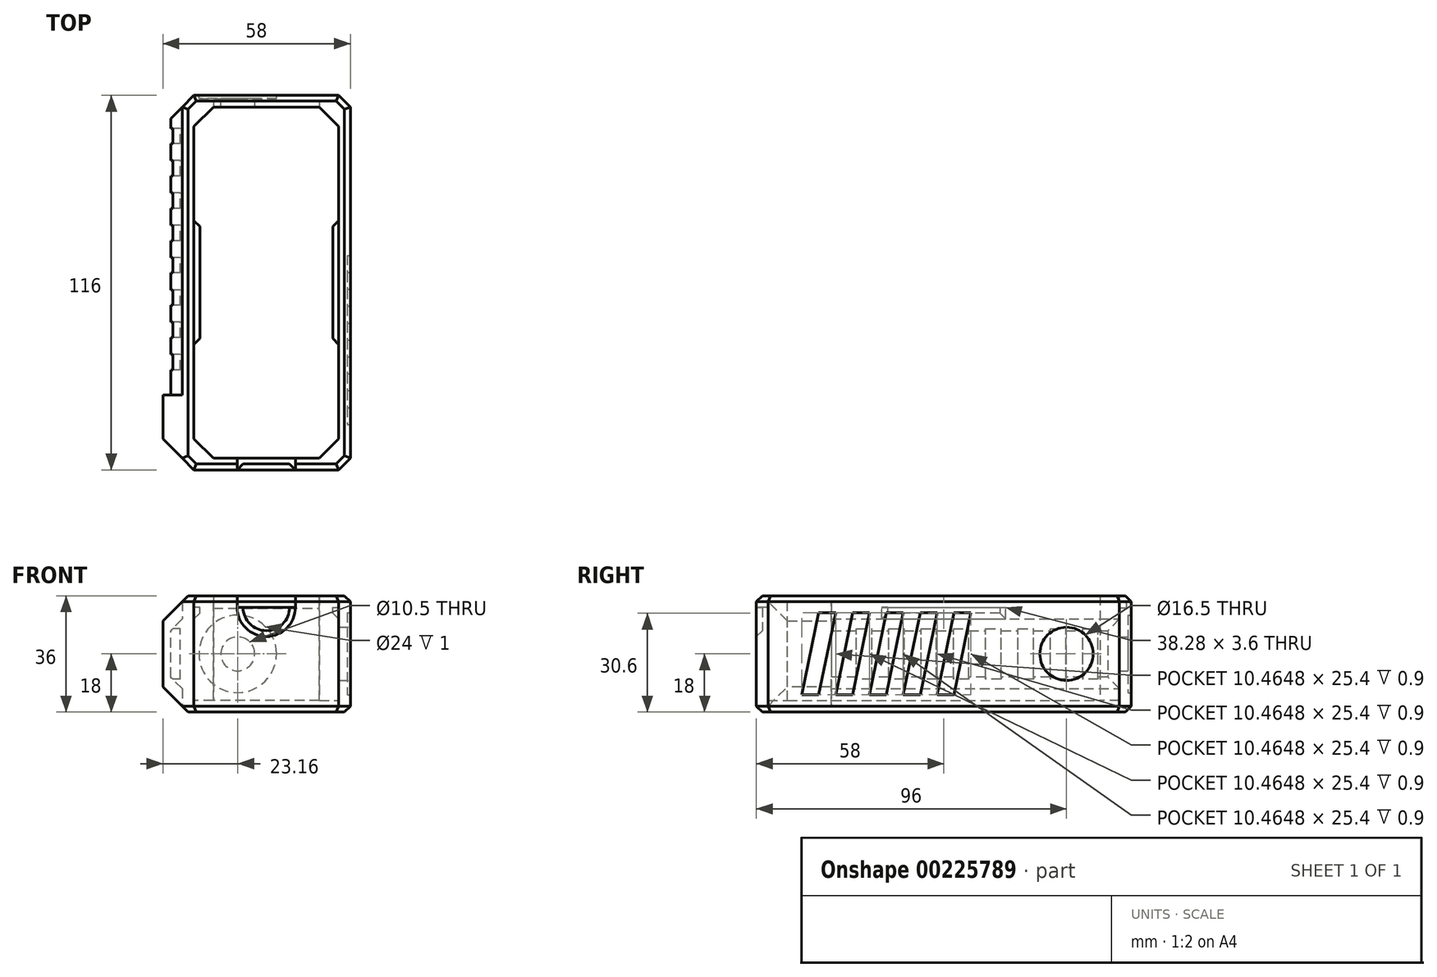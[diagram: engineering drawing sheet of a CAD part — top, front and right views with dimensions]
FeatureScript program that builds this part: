
annotation { "Feature Type Name" : "Feature", "Feature Type Description" : "" }
export const myFeature = defineFeature(function(context is Context, id is Id, definition is map)
    precondition{}
    {
        {
            assignVariable(context, id + "F0", {"name" : "O", "anyValue" : 3.6});
        }
        {
            assignVariable(context, id + "F1", {"name" : "H", "anyValue" : 36});
        }
        {
            var Q0;
            Q0=qCreatedBy(makeId("Top.planeOp"),FACE);
            var sketch = newSketch(context, id + "F2", { "sketchPlane" : qUnion([Q0])});
            skLineSegment(sketch, "E0.bottom", {"start": v(26, -58) * mm, "end": v(-26, -58) * mm});
            skLineSegment(sketch, "E0.top", {"start": v(26, 58) * mm, "end": v(-26, 58) * mm});
            skLineSegment(sketch, "E0.left", {"start": v(26, -58) * mm, "end": v(26, 58) * mm});
            skLineSegment(sketch, "E0.right", {"start": v(-26, -58) * mm, "end": v(-26, 58) * mm});
            skPoint(sketch, "E0.middle", {"position": v(0, 0) * mm});
            skLineSegment(sketch, "E1.0", {"start": v(22.4, 54.4) * mm, "end": v(-22.4, 54.4) * mm});
            skLineSegment(sketch, "E1.1", {"start": v(22.4, -54.4) * mm, "end": v(22.4, 54.4) * mm});
            skLineSegment(sketch, "E1.2", {"start": v(22.4, -54.4) * mm, "end": v(-22.4, -54.4) * mm});
            skLineSegment(sketch, "E1.3", {"start": v(-22.4, -54.4) * mm, "end": v(-22.4, 54.4) * mm});
            skSolve(sketch);
        }
        {
            var Q0;
            Q0=makeQuery(id+"F2.imprint","IMPRINT",FACE,{"disambiguationData":[TD([[makeQuery(id+"F2.imprint","IMPRINT",EDGE,{"derivedFrom":sQuery(id+"F2.wireOp",EDGE,"E0.bottom")}),-1.0]])]});
            extrude(context, id + "F3", {"entities" : qUnion([Q0]), "depth" : (getVariable(context, 'H')) * mm});
        }
        {
            var Q0;
            Q0=makeQuery(id+"F2.imprint","IMPRINT",FACE,{"disambiguationData":[TD([[makeQuery(id+"F2.imprint","IMPRINT",EDGE,{"derivedFrom":sQuery(id+"F2.wireOp",EDGE,"E1.0")}),1.0]])]});
            extrude(context, id + "F4", {"entities" : qUnion([Q0]), "operationType" : NewBodyOperationType.ADD, "depth" : (getVariable(context, 'O')) * mm});
        }
        {
            var Q0;
            Q0=makeQuery(id+"F3.opExtrude","SWEPT_FACE",FACE,{"disambiguationData":[OSD([sQuery(id+"F2.wireOp",EDGE,"E0.left")])]});
            var sketch = newSketch(context, id + "F5", { "sketchPlane" : qUnion([Q0])});
            skCircle(sketch, "E2", {"center": v(38, 18) * mm, "radius": 8.25 * mm});
            skSolve(sketch);
        }
        {
            var Q0;
            Q0=makeQuery(id+"F3.opExtrude","SWEPT_FACE",FACE,{"disambiguationData":[OSD([sQuery(id+"F2.wireOp",EDGE,"E0.top")])]});
            var sketch = newSketch(context, id + "F6", { "sketchPlane" : qUnion([Q0])});
            skCircle(sketch, "E3", {"center": v(8.84, 18) * mm, "radius": 5.25 * mm});
            skCircle(sketch, "E4", {"center": v(8.84, 18) * mm, "radius": 12 * mm});
            skSolve(sketch);
        }
        {
            var Q0;
            Q0=makeQuery(id+"F3.opExtrude","SWEPT_EDGE",EDGE,{"disambiguationData":[OSD([sQuery(id+"F2.wireOp",EDGE,"E0.bottom"),sQuery(id+"F2.wireOp",EDGE,"E0.right")])]});
            var Q1;
            Q1=makeQuery(id+"F3.opExtrude","SWEPT_EDGE",EDGE,{"disambiguationData":[OSD([sQuery(id+"F2.wireOp",EDGE,"E0.bottom"),sQuery(id+"F2.wireOp",EDGE,"E0.left")])]});
            var Q2;
            Q2=makeQuery(id+"F3.opExtrude","SWEPT_EDGE",EDGE,{"disambiguationData":[OSD([sQuery(id+"F2.wireOp",EDGE,"E0.top"),sQuery(id+"F2.wireOp",EDGE,"E0.left")])]});
            var Q3;
            Q3=makeQuery(id+"F3.opExtrude","SWEPT_EDGE",EDGE,{"disambiguationData":[OSD([sQuery(id+"F2.wireOp",EDGE,"E0.top"),sQuery(id+"F2.wireOp",EDGE,"E0.right")])]});
            chamfer(context, id + "F7", {"entities" : qUnion([Q0, Q1, Q2, Q3]), "width" : (getVariable(context, 'O')) * mm, "tangentPropagation" : true});
        }
        {
            var Q0;
            Q0=makeQuery(id+"F3.opExtrude","SWEPT_EDGE",EDGE,{"disambiguationData":[OSD([sQuery(id+"F2.wireOp",EDGE,"E1.0"),sQuery(id+"F2.wireOp",EDGE,"E1.3")])]});
            var Q1;
            Q1=makeQuery(id+"F3.opExtrude","SWEPT_EDGE",EDGE,{"disambiguationData":[OSD([sQuery(id+"F2.wireOp",EDGE,"E1.0"),sQuery(id+"F2.wireOp",EDGE,"E1.1")])]});
            var Q2;
            Q2=makeQuery(id+"F3.opExtrude","SWEPT_EDGE",EDGE,{"disambiguationData":[OSD([sQuery(id+"F2.wireOp",EDGE,"E1.2"),sQuery(id+"F2.wireOp",EDGE,"E1.3")])]});
            var Q3;
            Q3=makeQuery(id+"F3.opExtrude","SWEPT_EDGE",EDGE,{"disambiguationData":[OSD([sQuery(id+"F2.wireOp",EDGE,"E1.1"),sQuery(id+"F2.wireOp",EDGE,"E1.2")])]});
            chamfer(context, id + "F8", {"entities" : qUnion([Q0, Q1, Q2, Q3]), "width" : (getVariable(context, 'O') * 1.67) * mm, "tangentPropagation" : true});
        }
        {
            var Q0;
            Q0=makeQuery(id+"F6.imprint","IMPRINT",FACE,{"disambiguationData":[TD([[makeQuery(id+"F6.imprint","IMPRINT",EDGE,{"derivedFrom":sQuery(id+"F6.wireOp",EDGE,"E3")}),1.0]])]});
            extrude(context, id + "F9", {"entities" : qUnion([Q0]), "operationType" : NewBodyOperationType.REMOVE, "oppositeDirection" : true, "depth" : (getVariable(context, 'O')) * mm});
        }
        {
            var Q0;
            Q0=makeQuery(id+"F5.imprint","IMPRINT",FACE,{"disambiguationData":[TD([[makeQuery(id+"F5.imprint","IMPRINT",EDGE,{"derivedFrom":sQuery(id+"F5.wireOp",EDGE,"E2")}),1.0]])]});
            extrude(context, id + "F10", {"entities" : qUnion([Q0]), "operationType" : NewBodyOperationType.REMOVE, "oppositeDirection" : true, "depth" : (getVariable(context, 'O')) * mm});
        }
        {
            var Q0;
            Q0=makeQuery(id+"F3.opExtrude","SWEPT_FACE",FACE,{"disambiguationData":[OSD([sQuery(id+"F2.wireOp",EDGE,"E0.bottom")])]});
            var sketch = newSketch(context, id + "F11", { "sketchPlane" : qUnion([Q0])});
            skLineSegment(sketch, "E5.bottom", {"start": v(9, 32.4) * mm, "end": v(-9, 32.4) * mm});
            skLineSegment(sketch, "E5.top", {"start": v(9, 36) * mm, "end": v(-9, 36) * mm});
            skLineSegment(sketch, "E5.left", {"start": v(9, 32.4) * mm, "end": v(9, 36) * mm});
            skLineSegment(sketch, "E5.right", {"start": v(-9, 32.4) * mm, "end": v(-9, 36) * mm});
            skPoint(sketch, "E5.middle", {"position": v(0, 34.2) * mm});
            skPoint(sketch, "E5.middle.positionSnap0", {"position": v(0, 0) * mm});
            skPoint(sketch, "E5.centerSnap0", {"position": v(0, 0) * mm});
            skArc(sketch, "E6", {"start": v(-9, 32.4) * mm, "mid": v(0, 23.4) * mm, "end": v(9, 32.4) * mm});
            skSolve(sketch);
        }
        {
            var Q0;
            Q0=makeQuery(id+"F11.imprint","IMPRINT",FACE,{"disambiguationData":[TD([[makeQuery(id+"F11.imprint","IMPRINT",EDGE,{"derivedFrom":sQuery(id+"F11.wireOp",EDGE,"E5.bottom")}),-1.0]])]});
            extrude(context, id + "F12", {"entities" : qUnion([Q0]), "operationType" : NewBodyOperationType.REMOVE, "oppositeDirection" : true, "depth" : (getVariable(context, 'O')) * mm});
        }
        {
            var Q0;
            Q0=makeQuery(id+"F3.opExtrude","SWEPT_FACE",FACE,{"disambiguationData":[OSD([sQuery(id+"F2.wireOp",EDGE,"E1.0")])]});
            var sketch = newSketch(context, id + "F13", { "sketchPlane" : qUnion([Q0])});
            skLineSegment(sketch, "E7.bottom", {"start": v(-16.4, 34.2) * mm, "end": v(16.4, 34.2) * mm});
            skLineSegment(sketch, "E7.top", {"start": v(-16.4, 32.2) * mm, "end": v(16.4, 32.2) * mm});
            skLineSegment(sketch, "E7.left", {"start": v(-16.4, 34.2) * mm, "end": v(-16.4, 32.2) * mm});
            skLineSegment(sketch, "E7.right", {"start": v(16.4, 34.2) * mm, "end": v(16.4, 32.2) * mm});
            skSolve(sketch);
        }
        {
            var Q0;
            Q0=makeQuery(id+"F13.imprint","IMPRINT",FACE,{"disambiguationData":[TD([[makeQuery(id+"F13.imprint","IMPRINT",EDGE,{"derivedFrom":sQuery(id+"F13.wireOp",EDGE,"E7.bottom")}),-1.0]])]});
            extrude(context, id + "F14", {"entities" : qUnion([Q0]), "operationType" : NewBodyOperationType.REMOVE, "oppositeDirection" : true, "depth" : 2.1 * mm});
        }
        {
            var Q0;
            Q0=makeQuery(id+"F6.imprint","IMPRINT",FACE,{"disambiguationData":[TD([[makeQuery(id+"F6.imprint","IMPRINT",EDGE,{"derivedFrom":sQuery(id+"F6.wireOp",EDGE,"E3")}),-1.0]])]});
            extrude(context, id + "F15", {"entities" : qUnion([Q0]), "operationType" : NewBodyOperationType.REMOVE, "oppositeDirection" : true, "depth" : 1 * mm});
        }
        {
            var Q0;
            Q0=makeQuery(id+"F14.boolean.opBoolean","COPY",EDGE,{"derivedFrom":makeQuery(id+"F14.opExtrude","CAP_EDGE",EDGE,{"disambiguationData":[OSD([sQuery(id+"F13.wireOp",EDGE,"E7.bottom")])],"isStart":false})});
            fillet(context, id + "F16", {"entities" : qUnion([Q0]), "radius" : 0.5 * mm, "tangentPropagation" : true, "allowEdgeOverflow" : false});
        }
        {
            var Q0;
            Q0=makeQuery(id+"F3.opExtrude","SWEPT_FACE",FACE,{"disambiguationData":[OSD([sQuery(id+"F2.wireOp",EDGE,"E1.1")])]});
            var sketch = newSketch(context, id + "F17", { "sketchPlane" : qUnion([Q0])});
            skLineSegment(sketch, "E8.bottom", {"start": v(19.14, 28.8) * mm, "end": v(-19.14, 28.8) * mm});
            skLineSegment(sketch, "E8.top", {"start": v(19.14, 32.4) * mm, "end": v(-19.14, 32.4) * mm});
            skLineSegment(sketch, "E8.left", {"start": v(19.14, 28.8) * mm, "end": v(19.14, 32.4) * mm});
            skLineSegment(sketch, "E8.right", {"start": v(-19.14, 28.8) * mm, "end": v(-19.14, 32.4) * mm});
            skPoint(sketch, "E8.middle", {"position": v(0, 30.6) * mm});
            skSolve(sketch);
        }
        {
            var Q0;
            Q0=makeQuery(id+"F3.opExtrude","SWEPT_FACE",FACE,{"disambiguationData":[OSD([sQuery(id+"F2.wireOp",EDGE,"E1.3")])]});
            var sketch = newSketch(context, id + "F18", { "sketchPlane" : qUnion([Q0])});
            skLineSegment(sketch, "E9.bottom", {"start": v(19.14, 28.8) * mm, "end": v(-19.14, 28.8) * mm});
            skLineSegment(sketch, "E9.top", {"start": v(19.14, 32.4) * mm, "end": v(-19.14, 32.4) * mm});
            skLineSegment(sketch, "E9.left", {"start": v(19.14, 28.8) * mm, "end": v(19.14, 32.4) * mm});
            skLineSegment(sketch, "E9.right", {"start": v(-19.14, 28.8) * mm, "end": v(-19.14, 32.4) * mm});
            skPoint(sketch, "E9.middle", {"position": v(0, 30.6) * mm});
            skSolve(sketch);
        }
        {
            var Q0;
            Q0=makeQuery(id+"F17.imprint","IMPRINT",FACE,{"disambiguationData":[TD([[makeQuery(id+"F17.imprint","IMPRINT",EDGE,{"derivedFrom":sQuery(id+"F17.wireOp",EDGE,"E8.bottom")}),-1.0]])]});
            extrude(context, id + "F19", {"entities" : qUnion([Q0]), "operationType" : NewBodyOperationType.ADD, "depth" : (getVariable(context, 'O') * .5) * mm});
        }
        {
            var Q0;
            Q0=makeQuery(id+"F18.imprint","IMPRINT",FACE,{"disambiguationData":[TD([[makeQuery(id+"F18.imprint","IMPRINT",EDGE,{"derivedFrom":sQuery(id+"F18.wireOp",EDGE,"E9.bottom")}),-1.0]])]});
            extrude(context, id + "F20", {"entities" : qUnion([Q0]), "operationType" : NewBodyOperationType.ADD, "depth" : (getVariable(context, 'O') * .5) * mm});
        }
        {
            var Q0;
            Q0=makeQuery(id+"F20.opExtrude","CAP_EDGE",EDGE,{"disambiguationData":[OSD([sQuery(id+"F18.wireOp",EDGE,"E9.right")])],"isStart":false});
            var Q1;
            Q1=makeQuery(id+"F20.opExtrude","CAP_EDGE",EDGE,{"disambiguationData":[OSD([sQuery(id+"F18.wireOp",EDGE,"E9.bottom")])],"isStart":false});
            var Q2;
            Q2=makeQuery(id+"F20.opExtrude","CAP_EDGE",EDGE,{"disambiguationData":[OSD([sQuery(id+"F18.wireOp",EDGE,"E9.left")])],"isStart":false});
            var Q3;
            Q3=makeQuery(id+"FUkj4zLFzn2cjNl_1.opExtrude","CAP_EDGE",EDGE,{"disambiguationData":[OSD([sQuery(id+"FduqIQM7QhTX7Re_1.wireOp",EDGE,"Uwhg5jXr-3Yt5-poT9-xr3U-90L54EeIlBer.right")])],"isStart":false});
            var Q4;
            Q4=makeQuery(id+"FUkj4zLFzn2cjNl_1.opExtrude","CAP_EDGE",EDGE,{"disambiguationData":[OSD([sQuery(id+"FduqIQM7QhTX7Re_1.wireOp",EDGE,"Uwhg5jXr-3Yt5-poT9-xr3U-90L54EeIlBer.left")])],"isStart":false});
            var Q5;
            Q5=makeQuery(id+"FUkj4zLFzn2cjNl_1.opExtrude","CAP_EDGE",EDGE,{"disambiguationData":[OSD([sQuery(id+"FduqIQM7QhTX7Re_1.wireOp",EDGE,"Uwhg5jXr-3Yt5-poT9-xr3U-90L54EeIlBer.bottom")])],"isStart":false});
            var Q6;
            Q6=makeQuery(id+"F19.opExtrude","CAP_EDGE",EDGE,{"disambiguationData":[OSD([sQuery(id+"F17.wireOp",EDGE,"E8.right")])],"isStart":false});
            var Q7;
            Q7=makeQuery(id+"F19.opExtrude","CAP_EDGE",EDGE,{"disambiguationData":[OSD([sQuery(id+"F17.wireOp",EDGE,"E8.bottom")])],"isStart":false});
            var Q8;
            Q8=makeQuery(id+"F19.opExtrude","CAP_EDGE",EDGE,{"disambiguationData":[OSD([sQuery(id+"F17.wireOp",EDGE,"E8.left")])],"isStart":false});
            chamfer(context, id + "F21", {"entities" : qUnion([Q0, Q1, Q2, Q3, Q4, Q5, Q6, Q7, Q8]), "width" : (getVariable(context, 'O') * 0.5) * mm, "tangentPropagation" : true});
        }
        {
            var Q0;
            Q0=makeQuery(id+"F3.opExtrude","SWEPT_FACE",FACE,{"disambiguationData":[OSD([sQuery(id+"F2.wireOp",EDGE,"E1.2")])]});
            var sketch = newSketch(context, id + "F22", { "sketchPlane" : qUnion([Q0])});
            skSolve(sketch);
        }
        {
            var Q0;
            Q0=makeQuery(id+"F11.imprint","IMPRINT",FACE,{"disambiguationData":[TD([[makeQuery(id+"F11.imprint","IMPRINT",EDGE,{"derivedFrom":sQuery(id+"F11.wireOp",EDGE,"E5.bottom")}),1.0]])]});
            extrude(context, id + "F23", {"entities" : qUnion([Q0]), "operationType" : NewBodyOperationType.REMOVE, "oppositeDirection" : true, "depth" : (getVariable(context, 'O') / 2) * mm});
        }
        {
            var Q0;
            Q0=makeQuery(id+"F23.boolean.opBoolean","COPY",EDGE,{"derivedFrom":makeQuery(id+"F23.opExtrude","CAP_EDGE",EDGE,{"disambiguationData":[OSD([sQuery(id+"F11.wireOp",EDGE,"E6")])],"isStart":false})});
            chamfer(context, id + "F24", {"entities" : qUnion([Q0]), "width" : 1.8 * mm, "tangentPropagation" : true});
        }
        {
            var Q0;
            {var subQ0=sQuery(id+"F2.wireOp",EDGE,"E0.bottom");Q0=makeQuery(id+"F12.boolean.opBoolean","SPLIT",EDGE,{"disambiguationData":[TD([makeQuery(id+"F12.opExtrude","SWEPT_FACE",FACE,{"disambiguationData":[OSD([sQuery(id+"F11.wireOp",EDGE,"E5.right")])]})])],"derivedFrom":makeQuery(id+"F3.opExtrude","CAP_EDGE",EDGE,{"disambiguationData":[OSD([subQ0])],"isStart":false})});}
            var Q1;
            {var subQ0=sQuery(id+"F2.wireOp",EDGE,"E0.right");var subQ1=sQuery(id+"F2.wireOp",EDGE,"E0.bottom");Q1=makeQuery(id+"F7.opChamfer","BLEND_EDGE",EDGE,{"blendedFrom":[makeQuery(id+"F3.opExtrude","SWEPT_EDGE",EDGE,{"disambiguationData":[OSD([subQ1,subQ0])]}),makeQuery(id+"F3.opExtrude","CAP_FACE",FACE,{"disambiguationData":[OSD([subQ1,sQuery(id+"F2.wireOp",EDGE,"E0.top"),sQuery(id+"F2.wireOp",EDGE,"E0.left"),subQ0,sQuery(id+"F2.wireOp",EDGE,"E1.0"),sQuery(id+"F2.wireOp",EDGE,"E1.1"),sQuery(id+"F2.wireOp",EDGE,"E1.2"),sQuery(id+"F2.wireOp",EDGE,"E1.3")])],"isStart":false})],"blendedInto":[makeQuery(id+"F3.opExtrude","CAP_FACE",FACE,{"disambiguationData":[OSD([subQ1,sQuery(id+"F2.wireOp",EDGE,"E0.top"),sQuery(id+"F2.wireOp",EDGE,"E0.left"),subQ0,sQuery(id+"F2.wireOp",EDGE,"E1.0"),sQuery(id+"F2.wireOp",EDGE,"E1.1"),sQuery(id+"F2.wireOp",EDGE,"E1.2"),sQuery(id+"F2.wireOp",EDGE,"E1.3")])],"isStart":false})]});}
            var Q2;
            Q2=makeQuery(id+"F3.opExtrude","CAP_EDGE",EDGE,{"disambiguationData":[OSD([sQuery(id+"F2.wireOp",EDGE,"E0.right")])],"isStart":false});
            var Q3;
            {var subQ0=sQuery(id+"F2.wireOp",EDGE,"E0.right");var subQ1=sQuery(id+"F2.wireOp",EDGE,"E0.top");Q3=makeQuery(id+"F7.opChamfer","BLEND_EDGE",EDGE,{"blendedFrom":[makeQuery(id+"F3.opExtrude","SWEPT_EDGE",EDGE,{"disambiguationData":[OSD([subQ1,subQ0])]}),makeQuery(id+"F3.opExtrude","CAP_FACE",FACE,{"disambiguationData":[OSD([sQuery(id+"F2.wireOp",EDGE,"E0.bottom"),subQ1,sQuery(id+"F2.wireOp",EDGE,"E0.left"),subQ0,sQuery(id+"F2.wireOp",EDGE,"E1.0"),sQuery(id+"F2.wireOp",EDGE,"E1.1"),sQuery(id+"F2.wireOp",EDGE,"E1.2"),sQuery(id+"F2.wireOp",EDGE,"E1.3")])],"isStart":false})],"blendedInto":[makeQuery(id+"F3.opExtrude","CAP_FACE",FACE,{"disambiguationData":[OSD([sQuery(id+"F2.wireOp",EDGE,"E0.bottom"),subQ1,sQuery(id+"F2.wireOp",EDGE,"E0.left"),subQ0,sQuery(id+"F2.wireOp",EDGE,"E1.0"),sQuery(id+"F2.wireOp",EDGE,"E1.1"),sQuery(id+"F2.wireOp",EDGE,"E1.2"),sQuery(id+"F2.wireOp",EDGE,"E1.3")])],"isStart":false})]});}
            var Q4;
            Q4=makeQuery(id+"F3.opExtrude","CAP_EDGE",EDGE,{"disambiguationData":[OSD([sQuery(id+"F2.wireOp",EDGE,"E0.top")])],"isStart":false});
            var Q5;
            {var subQ0=sQuery(id+"F2.wireOp",EDGE,"E0.left");var subQ1=sQuery(id+"F2.wireOp",EDGE,"E0.top");Q5=makeQuery(id+"F7.opChamfer","BLEND_EDGE",EDGE,{"blendedFrom":[makeQuery(id+"F3.opExtrude","SWEPT_EDGE",EDGE,{"disambiguationData":[OSD([subQ1,subQ0])]}),makeQuery(id+"F3.opExtrude","CAP_FACE",FACE,{"disambiguationData":[OSD([sQuery(id+"F2.wireOp",EDGE,"E0.bottom"),subQ1,subQ0,sQuery(id+"F2.wireOp",EDGE,"E0.right"),sQuery(id+"F2.wireOp",EDGE,"E1.0"),sQuery(id+"F2.wireOp",EDGE,"E1.1"),sQuery(id+"F2.wireOp",EDGE,"E1.2"),sQuery(id+"F2.wireOp",EDGE,"E1.3")])],"isStart":false})],"blendedInto":[makeQuery(id+"F3.opExtrude","CAP_FACE",FACE,{"disambiguationData":[OSD([sQuery(id+"F2.wireOp",EDGE,"E0.bottom"),subQ1,subQ0,sQuery(id+"F2.wireOp",EDGE,"E0.right"),sQuery(id+"F2.wireOp",EDGE,"E1.0"),sQuery(id+"F2.wireOp",EDGE,"E1.1"),sQuery(id+"F2.wireOp",EDGE,"E1.2"),sQuery(id+"F2.wireOp",EDGE,"E1.3")])],"isStart":false})]});}
            var Q6;
            Q6=makeQuery(id+"F3.opExtrude","CAP_EDGE",EDGE,{"disambiguationData":[OSD([sQuery(id+"F2.wireOp",EDGE,"E0.left")])],"isStart":false});
            var Q7;
            {var subQ0=sQuery(id+"F2.wireOp",EDGE,"E0.left");var subQ1=sQuery(id+"F2.wireOp",EDGE,"E0.bottom");Q7=makeQuery(id+"F7.opChamfer","BLEND_EDGE",EDGE,{"blendedFrom":[makeQuery(id+"F3.opExtrude","SWEPT_EDGE",EDGE,{"disambiguationData":[OSD([subQ1,subQ0])]}),makeQuery(id+"F3.opExtrude","CAP_FACE",FACE,{"disambiguationData":[OSD([subQ1,sQuery(id+"F2.wireOp",EDGE,"E0.top"),subQ0,sQuery(id+"F2.wireOp",EDGE,"E0.right"),sQuery(id+"F2.wireOp",EDGE,"E1.0"),sQuery(id+"F2.wireOp",EDGE,"E1.1"),sQuery(id+"F2.wireOp",EDGE,"E1.2"),sQuery(id+"F2.wireOp",EDGE,"E1.3")])],"isStart":false})],"blendedInto":[makeQuery(id+"F3.opExtrude","CAP_FACE",FACE,{"disambiguationData":[OSD([subQ1,sQuery(id+"F2.wireOp",EDGE,"E0.top"),subQ0,sQuery(id+"F2.wireOp",EDGE,"E0.right"),sQuery(id+"F2.wireOp",EDGE,"E1.0"),sQuery(id+"F2.wireOp",EDGE,"E1.1"),sQuery(id+"F2.wireOp",EDGE,"E1.2"),sQuery(id+"F2.wireOp",EDGE,"E1.3")])],"isStart":false})]});}
            var Q8;
            {var subQ0=sQuery(id+"F2.wireOp",EDGE,"E0.bottom");Q8=makeQuery(id+"F12.boolean.opBoolean","SPLIT",EDGE,{"disambiguationData":[TD([makeQuery(id+"F12.opExtrude","SWEPT_FACE",FACE,{"disambiguationData":[OSD([sQuery(id+"F11.wireOp",EDGE,"E5.left")])]})])],"derivedFrom":makeQuery(id+"F3.opExtrude","CAP_EDGE",EDGE,{"disambiguationData":[OSD([subQ0])],"isStart":false})});}
            var Q9;
            {var subQ0=sQuery(id+"F2.wireOp",EDGE,"E1.3");var subQ1=sQuery(id+"F2.wireOp",EDGE,"E1.2");var subQ2=sQuery(id+"F2.wireOp",EDGE,"E1.1");var subQ3=sQuery(id+"F2.wireOp",EDGE,"E1.0");Q9=makeQuery(id+"F4.boolean.opBoolean","MERGE",FACE,{"derivedFrom":[makeQuery(id+"F3.opExtrude","CAP_FACE",FACE,{"disambiguationData":[OSD([sQuery(id+"F2.wireOp",EDGE,"E0.bottom"),sQuery(id+"F2.wireOp",EDGE,"E0.top"),sQuery(id+"F2.wireOp",EDGE,"E0.left"),sQuery(id+"F2.wireOp",EDGE,"E0.right"),subQ3,subQ2,subQ1,subQ0])],"isStart":true}),makeQuery(id+"F4.opExtrude","CAP_FACE",FACE,{"disambiguationData":[OSD([subQ3,subQ2,subQ1,subQ0])],"isStart":true})]});}
            chamfer(context, id + "F25", {"entities" : qUnion([Q0, Q1, Q2, Q3, Q4, Q5, Q6, Q7, Q8, Q9]), "width" : (getVariable(context, 'O') / 2) * mm, "tangentPropagation" : true});
        }
        {
            var Q0;
            Q0=makeQuery(id+"F3.opExtrude","SWEPT_FACE",FACE,{"disambiguationData":[OSD([sQuery(id+"F2.wireOp",EDGE,"E0.right")])]});
            var sketch = newSketch(context, id + "F26", { "sketchPlane" : qUnion([Q0])});
            skLineSegment(sketch, "E10.bottom", {"start": v(54.4, 34.2) * mm, "end": v(34.8, 34.2) * mm});
            skLineSegment(sketch, "E10.top", {"start": v(54.4, 1.8) * mm, "end": v(34.8, 1.8) * mm});
            skLineSegment(sketch, "E10.left", {"start": v(54.4, 34.2) * mm, "end": v(54.4, 1.8) * mm});
            skLineSegment(sketch, "E10.right", {"start": v(34.8, 34.2) * mm, "end": v(34.8, 1.8) * mm});
            skLineSegment(sketch, "E11.bottom", {"start": v(34.8, 28.8) * mm, "end": v(-54.4, 28.8) * mm});
            skLineSegment(sketch, "E11.top", {"start": v(34.8, 7.2) * mm, "end": v(-54.4, 7.2) * mm});
            skLineSegment(sketch, "E11.left", {"start": v(34.8, 28.8) * mm, "end": v(34.8, 7.2) * mm});
            skLineSegment(sketch, "E11.right", {"start": v(-54.4, 28.8) * mm, "end": v(-54.4, 7.2) * mm});
            skSolve(sketch);
        }
        {
            var Q0;
            Q0=makeQuery(id+"F26.imprint","IMPRINT",FACE,{"disambiguationData":[TD([[makeQuery(id+"F26.imprint","IMPRINT",EDGE,{"derivedFrom":sQuery(id+"F26.wireOp",EDGE,"E11.bottom")}),1.0]])]});
            extrude(context, id + "F27", {"entities" : qUnion([Q0]), "operationType" : NewBodyOperationType.ADD, "depth" : (getVariable(context, 'O')) * mm});
        }
        {
            var Q0;
            {var subQ1=sQuery(id+"F26.wireOp",EDGE,"E10.bottom");Q0=makeQuery(id+"F26.imprint","IMPRINT",FACE,{"disambiguationData":[TD([[makeQuery(id+"F26.imprint","IMPRINT",EDGE,{"derivedFrom":subQ1}),1.0]])]});}
            extrude(context, id + "F28", {"entities" : qUnion([Q0]), "operationType" : NewBodyOperationType.ADD, "depth" : (getVariable(context, 'O') * 1.67) * mm});
        }
        {
            var Q0;
            Q0=makeQuery(id+"F27.opExtrude","CAP_FACE",FACE,{"disambiguationData":[OSD([sQuery(id+"F26.wireOp",EDGE,"E11.bottom"),sQuery(id+"F26.wireOp",EDGE,"E11.top"),sQuery(id+"F26.wireOp",EDGE,"E11.left"),sQuery(id+"F26.wireOp",EDGE,"E11.right")])],"isStart":false});
            var sketch = newSketch(context, id + "F29", { "sketchPlane" : qUnion([Q0])});
            skLineSegment(sketch, "E12.bottom", {"start": v(-43.01, 10.16) * mm, "end": v(-47.79, 10.16) * mm});
            skLineSegment(sketch, "E12.top", {"start": v(-43.01, 25.84) * mm, "end": v(-47.79, 25.84) * mm});
            skLineSegment(sketch, "E12.left", {"start": v(-43.01, 10.16) * mm, "end": v(-43.01, 25.84) * mm});
            skLineSegment(sketch, "E12.right", {"start": v(-47.79, 10.16) * mm, "end": v(-47.79, 25.84) * mm});
            skPoint(sketch, "E12.middle", {"position": v(-45.4, 18) * mm});
            skPoint(sketch, "E12.middle.positionSnap0", {"position": v(-54.4, 18) * mm});
            skPoint(sketch, "E12.centerSnap0", {"position": v(-54.4, 18) * mm});
            skLineSegment(sketch, "E13.1.0.0", {"start": v(-33, 10.16) * mm, "end": v(-33, 25.84) * mm});
            skLineSegment(sketch, "E13.1.0.1", {"start": v(-33, 25.84) * mm, "end": v(-37.78, 25.84) * mm});
            skLineSegment(sketch, "E13.1.0.2", {"start": v(-37.78, 10.16) * mm, "end": v(-37.78, 25.84) * mm});
            skLineSegment(sketch, "E13.1.0.3", {"start": v(-33, 10.16) * mm, "end": v(-37.78, 10.16) * mm});
            skLineSegment(sketch, "E13.2.0.0", {"start": v(-23, 10.16) * mm, "end": v(-23, 25.84) * mm});
            skLineSegment(sketch, "E13.2.0.1", {"start": v(-23, 25.84) * mm, "end": v(-27.78, 25.84) * mm});
            skLineSegment(sketch, "E13.2.0.2", {"start": v(-27.78, 10.16) * mm, "end": v(-27.78, 25.84) * mm});
            skLineSegment(sketch, "E13.2.0.3", {"start": v(-23, 10.16) * mm, "end": v(-27.78, 10.16) * mm});
            skLineSegment(sketch, "E13.3.0.0", {"start": v(-13, 10.16) * mm, "end": v(-13, 25.84) * mm});
            skLineSegment(sketch, "E13.3.0.1", {"start": v(-13, 25.84) * mm, "end": v(-17.77, 25.84) * mm});
            skLineSegment(sketch, "E13.3.0.2", {"start": v(-17.77, 10.16) * mm, "end": v(-17.77, 25.84) * mm});
            skLineSegment(sketch, "E13.3.0.3", {"start": v(-13, 10.16) * mm, "end": v(-17.77, 10.16) * mm});
            skLineSegment(sketch, "E13.4.0.0", {"start": v(-3, 10.16) * mm, "end": v(-3, 25.84) * mm});
            skLineSegment(sketch, "E13.4.0.1", {"start": v(-3, 25.84) * mm, "end": v(-7.77, 25.84) * mm});
            skLineSegment(sketch, "E13.4.0.2", {"start": v(-7.77, 10.16) * mm, "end": v(-7.77, 25.84) * mm});
            skLineSegment(sketch, "E13.4.0.3", {"start": v(-3, 10.16) * mm, "end": v(-7.77, 10.16) * mm});
            skLineSegment(sketch, "E13.5.0.0", {"start": v(7.01, 10.16) * mm, "end": v(7.01, 25.84) * mm});
            skLineSegment(sketch, "E13.5.0.1", {"start": v(7.01, 25.84) * mm, "end": v(2.24, 25.84) * mm});
            skLineSegment(sketch, "E13.5.0.2", {"start": v(2.24, 10.16) * mm, "end": v(2.24, 25.84) * mm});
            skLineSegment(sketch, "E13.5.0.3", {"start": v(7.01, 10.16) * mm, "end": v(2.24, 10.16) * mm});
            skLineSegment(sketch, "E13.6.0.0", {"start": v(17.02, 10.16) * mm, "end": v(17.02, 25.84) * mm});
            skLineSegment(sketch, "E13.6.0.1", {"start": v(17.02, 25.84) * mm, "end": v(12.24, 25.84) * mm});
            skLineSegment(sketch, "E13.6.0.2", {"start": v(12.24, 10.16) * mm, "end": v(12.24, 25.84) * mm});
            skLineSegment(sketch, "E13.6.0.3", {"start": v(17.02, 10.16) * mm, "end": v(12.24, 10.16) * mm});
            skLineSegment(sketch, "E13.7.0.0", {"start": v(27.02, 10.16) * mm, "end": v(27.02, 25.84) * mm});
            skLineSegment(sketch, "E13.7.0.1", {"start": v(27.02, 25.84) * mm, "end": v(22.25, 25.84) * mm});
            skLineSegment(sketch, "E13.7.0.2", {"start": v(22.25, 10.16) * mm, "end": v(22.25, 25.84) * mm});
            skLineSegment(sketch, "E13.7.0.3", {"start": v(27.02, 10.16) * mm, "end": v(22.25, 10.16) * mm});
            skLineSegment(sketch, "E13.direction1", {"start": v(-43.01, 10.16) * mm, "end": v(-33, 10.16) * mm, "construction": true});
            skSolve(sketch);
        }
        {
            var Q0;
            Q0=makeQuery(id+"F27.opExtrude","CAP_EDGE",EDGE,{"disambiguationData":[OSD([sQuery(id+"F26.wireOp",EDGE,"E11.right")])],"isStart":false});
            var Q1;
            Q1=makeQuery(id+"F27.opExtrude","CAP_EDGE",EDGE,{"disambiguationData":[OSD([sQuery(id+"F26.wireOp",EDGE,"E11.top")])],"isStart":false});
            var Q2;
            Q2=makeQuery(id+"F27.opExtrude","CAP_EDGE",EDGE,{"disambiguationData":[OSD([sQuery(id+"F26.wireOp",EDGE,"E11.bottom")])],"isStart":false});
            chamfer(context, id + "F30", {"entities" : qUnion([Q0, Q1, Q2]), "width" : (getVariable(context, 'O')) * mm, "tangentPropagation" : true});
        }
        {
            var Q0;
            Q0=makeQuery(id+"F29.imprint","IMPRINT",FACE,{"disambiguationData":[TD([[makeQuery(id+"F29.imprint","IMPRINT",EDGE,{"derivedFrom":sQuery(id+"F29.wireOp",EDGE,"E12.bottom")}),-1.0]])]});
            var Q1;
            Q1=makeQuery(id+"F29.imprint","IMPRINT",FACE,{"disambiguationData":[TD([[makeQuery(id+"F29.imprint","IMPRINT",EDGE,{"derivedFrom":sQuery(id+"F29.wireOp",EDGE,"E13.1.0.0")}),1.0]])]});
            var Q2;
            Q2=makeQuery(id+"F29.imprint","IMPRINT",FACE,{"disambiguationData":[TD([[makeQuery(id+"F29.imprint","IMPRINT",EDGE,{"derivedFrom":sQuery(id+"F29.wireOp",EDGE,"E13.2.0.0")}),1.0]])]});
            var Q3;
            Q3=makeQuery(id+"F29.imprint","IMPRINT",FACE,{"disambiguationData":[TD([[makeQuery(id+"F29.imprint","IMPRINT",EDGE,{"derivedFrom":sQuery(id+"F29.wireOp",EDGE,"E13.3.0.0")}),1.0]])]});
            var Q4;
            Q4=makeQuery(id+"F29.imprint","IMPRINT",FACE,{"disambiguationData":[TD([[makeQuery(id+"F29.imprint","IMPRINT",EDGE,{"derivedFrom":sQuery(id+"F29.wireOp",EDGE,"E13.4.0.0")}),1.0]])]});
            var Q5;
            Q5=makeQuery(id+"F29.imprint","IMPRINT",FACE,{"disambiguationData":[TD([[makeQuery(id+"F29.imprint","IMPRINT",EDGE,{"derivedFrom":sQuery(id+"F29.wireOp",EDGE,"E13.5.0.0")}),1.0]])]});
            var Q6;
            Q6=makeQuery(id+"F29.imprint","IMPRINT",FACE,{"disambiguationData":[TD([[makeQuery(id+"F29.imprint","IMPRINT",EDGE,{"derivedFrom":sQuery(id+"F29.wireOp",EDGE,"E13.6.0.0")}),1.0]])]});
            var Q7;
            Q7=makeQuery(id+"F29.imprint","IMPRINT",FACE,{"disambiguationData":[TD([[makeQuery(id+"F29.imprint","IMPRINT",EDGE,{"derivedFrom":sQuery(id+"F29.wireOp",EDGE,"E13.7.0.0")}),1.0]])]});
            extrude(context, id + "F31", {"entities" : qUnion([Q0, Q1, Q2, Q3, Q4, Q5, Q6, Q7]), "operationType" : NewBodyOperationType.REMOVE, "oppositeDirection" : true, "depth" : 3 * mm});
        }
        {
            var Q0;
            Q0=makeQuery(id+"F28.opExtrude","CAP_EDGE",EDGE,{"disambiguationData":[OSD([sQuery(id+"F26.wireOp",EDGE,"E10.bottom")])],"isStart":false});
            var Q1;
            Q1=makeQuery(id+"F28.opExtrude","CAP_EDGE",EDGE,{"disambiguationData":[OSD([sQuery(id+"F26.wireOp",EDGE,"E10.left")])],"isStart":false});
            var Q2;
            Q2=makeQuery(id+"F28.opExtrude","CAP_EDGE",EDGE,{"disambiguationData":[OSD([sQuery(id+"F26.wireOp",EDGE,"E10.top")])],"isStart":false});
            chamfer(context, id + "F32", {"entities" : qUnion([Q0, Q1, Q2]), "width" : (getVariable(context, 'O') * 1.67) * mm, "tangentPropagation" : true});
        }
        {
            var Q0;
            Q0=makeQuery(id+"F3.opExtrude","SWEPT_FACE",FACE,{"disambiguationData":[OSD([sQuery(id+"F2.wireOp",EDGE,"E0.left")])]});
            var sketch = newSketch(context, id + "F33", { "sketchPlane" : qUnion([Q0])});
            skLineSegment(sketch, "E14", {"start": v(-38.7, 30.7) * mm, "end": v(-43.94, 5.3) * mm});
            skLineSegment(sketch, "E15", {"start": v(-43.94, 5.3) * mm, "end": v(-38.7, 5.3) * mm});
            skLineSegment(sketch, "E16", {"start": v(-38.7, 5.3) * mm, "end": v(-33.47, 30.7) * mm});
            skLineSegment(sketch, "E17", {"start": v(-33.47, 30.7) * mm, "end": v(-38.7, 30.7) * mm});
            skLineSegment(sketch, "E18.1.0.0", {"start": v(-28.24, 30.7) * mm, "end": v(-33.47, 5.3) * mm});
            skLineSegment(sketch, "E18.1.0.1", {"start": v(-23, 30.7) * mm, "end": v(-28.24, 30.7) * mm});
            skLineSegment(sketch, "E18.1.0.2", {"start": v(-28.24, 5.3) * mm, "end": v(-23, 30.7) * mm});
            skLineSegment(sketch, "E18.1.0.3", {"start": v(-33.47, 5.3) * mm, "end": v(-28.24, 5.3) * mm});
            skLineSegment(sketch, "E18.2.0.0", {"start": v(-17.77, 30.7) * mm, "end": v(-23, 5.3) * mm});
            skLineSegment(sketch, "E18.2.0.1", {"start": v(-12.54, 30.7) * mm, "end": v(-17.77, 30.7) * mm});
            skLineSegment(sketch, "E18.2.0.2", {"start": v(-17.77, 5.3) * mm, "end": v(-12.54, 30.7) * mm});
            skLineSegment(sketch, "E18.2.0.3", {"start": v(-23, 5.3) * mm, "end": v(-17.77, 5.3) * mm});
            skLineSegment(sketch, "E18.3.0.0", {"start": v(-7.3, 30.7) * mm, "end": v(-12.54, 5.3) * mm});
            skLineSegment(sketch, "E18.3.0.1", {"start": v(-2.08, 30.7) * mm, "end": v(-7.3, 30.7) * mm});
            skLineSegment(sketch, "E18.3.0.2", {"start": v(-7.3, 5.3) * mm, "end": v(-2.08, 30.7) * mm});
            skLineSegment(sketch, "E18.3.0.3", {"start": v(-12.54, 5.3) * mm, "end": v(-7.3, 5.3) * mm});
            skLineSegment(sketch, "E18.4.0.0", {"start": v(3.16, 30.7) * mm, "end": v(-2.08, 5.3) * mm});
            skLineSegment(sketch, "E18.4.0.1", {"start": v(8.39, 30.7) * mm, "end": v(3.16, 30.7) * mm});
            skLineSegment(sketch, "E18.4.0.2", {"start": v(3.16, 5.3) * mm, "end": v(8.39, 30.7) * mm});
            skLineSegment(sketch, "E18.4.0.3", {"start": v(-2.08, 5.3) * mm, "end": v(3.16, 5.3) * mm});
            skLineSegment(sketch, "E18.direction1", {"start": v(-43.94, 5.3) * mm, "end": v(-33.47, 5.3) * mm, "construction": true});
            skSolve(sketch);
        }
        {
            var Q0;
            Q0=makeQuery(id+"F33.imprint","IMPRINT",FACE,{"disambiguationData":[TD([[makeQuery(id+"F33.imprint","IMPRINT",EDGE,{"derivedFrom":sQuery(id+"F33.wireOp",EDGE,"E14")}),1.0]])]});
            var Q1;
            Q1=makeQuery(id+"F33.imprint","IMPRINT",FACE,{"disambiguationData":[TD([[makeQuery(id+"F33.imprint","IMPRINT",EDGE,{"derivedFrom":sQuery(id+"F33.wireOp",EDGE,"E18.1.0.0")}),1.0]])]});
            var Q2;
            Q2=makeQuery(id+"F33.imprint","IMPRINT",FACE,{"disambiguationData":[TD([[makeQuery(id+"F33.imprint","IMPRINT",EDGE,{"derivedFrom":sQuery(id+"F33.wireOp",EDGE,"E18.2.0.0")}),1.0]])]});
            var Q3;
            Q3=makeQuery(id+"F33.imprint","IMPRINT",FACE,{"disambiguationData":[TD([[makeQuery(id+"F33.imprint","IMPRINT",EDGE,{"derivedFrom":sQuery(id+"F33.wireOp",EDGE,"E18.3.0.0")}),1.0]])]});
            var Q4;
            Q4=makeQuery(id+"F33.imprint","IMPRINT",FACE,{"disambiguationData":[TD([[makeQuery(id+"F33.imprint","IMPRINT",EDGE,{"derivedFrom":sQuery(id+"F33.wireOp",EDGE,"E18.4.0.0")}),1.0]])]});
            extrude(context, id + "F34", {"entities" : qUnion([Q0, Q1, Q2, Q3, Q4]), "operationType" : NewBodyOperationType.REMOVE, "oppositeDirection" : true, "depth" : .9 * mm});
        }
    });
